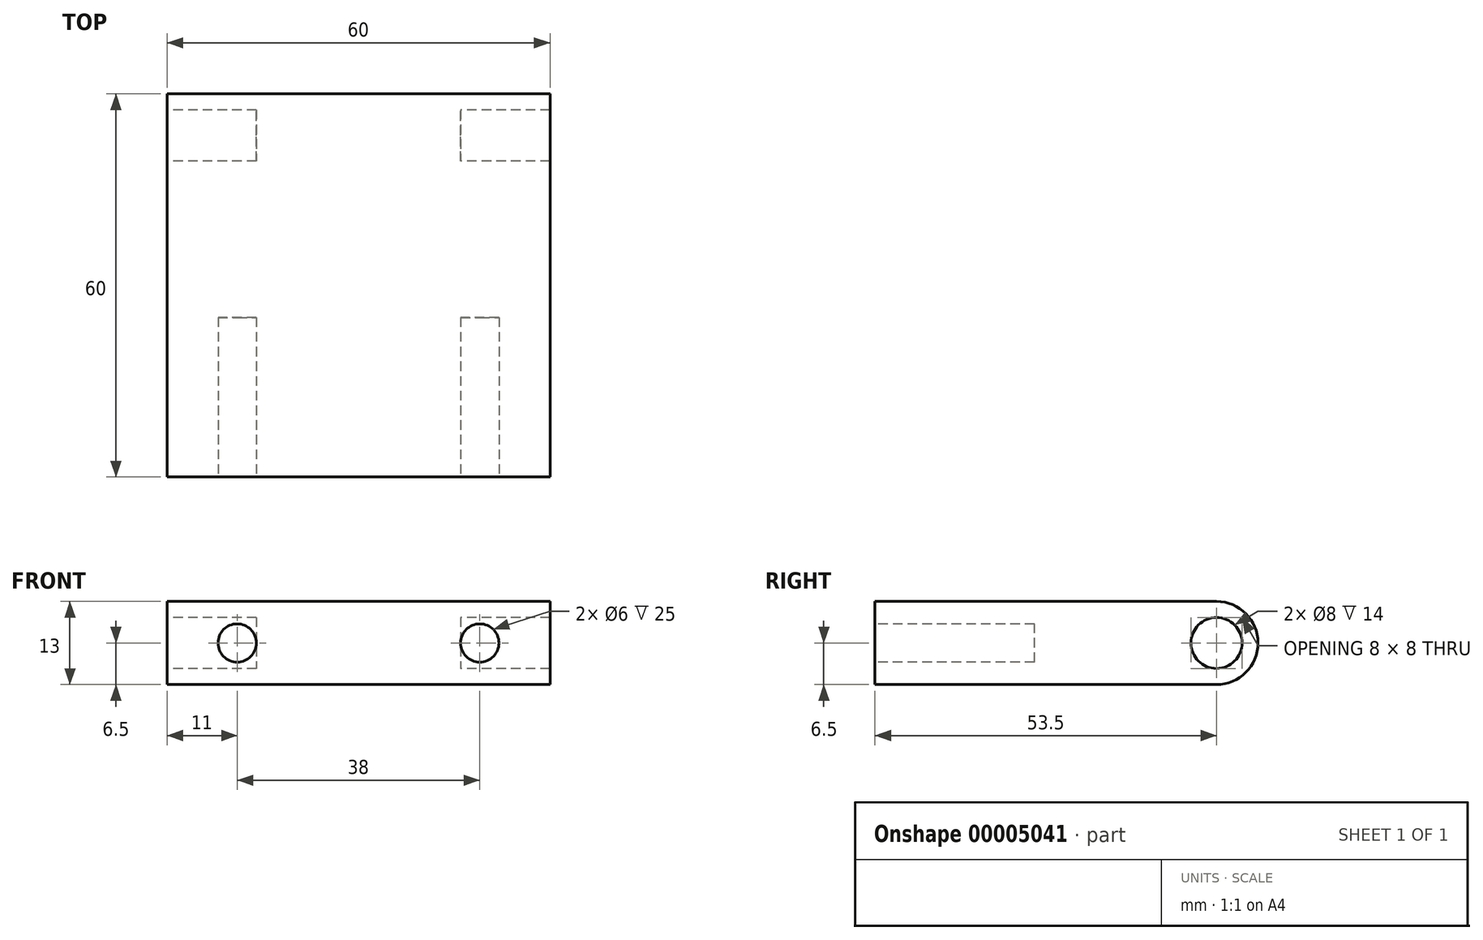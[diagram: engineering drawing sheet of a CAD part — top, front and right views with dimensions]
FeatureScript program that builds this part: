
annotation { "Feature Type Name" : "Feature", "Feature Type Description" : "" }
export const myFeature = defineFeature(function(context is Context, id is Id, definition is map)
    precondition{}
    {
        {
            var Q0;
            Q0=qCreatedBy(makeId("Top.planeOp"),FACE);
            var sketch = newSketch(context, id + "F0", { "sketchPlane" : qUnion([Q0])});
            skLineSegment(sketch, "E0.rect.bottom", {"start": v(30, 30) * mm, "end": v(-30, 30) * mm});
            skLineSegment(sketch, "E0.rect.top", {"start": v(30, -30) * mm, "end": v(-30, -30) * mm});
            skLineSegment(sketch, "E0.rect.left", {"start": v(30, 30) * mm, "end": v(30, -30) * mm});
            skLineSegment(sketch, "E0.rect.right", {"start": v(-30, 30) * mm, "end": v(-30, -30) * mm});
            skPoint(sketch, "E0.rect.middle", {"position": v(0, 0) * mm});
            skSolve(sketch);
        }
        {
            var Q0;
            Q0=makeQuery(id+"F0.imprint","IMPRINT",FACE,{"disambiguationData":[TD([[makeQuery(id+"F0.imprint","IMPRINT",EDGE,{"derivedFrom":sQuery(id+"F0.wireOp",EDGE,"E0.rect.bottom")}),1.0]])]});
            extrude(context, id + "F1", {"entities" : qUnion([Q0]), "depth" : 13 * mm});
        }
        {
            var Q0;
            Q0=makeQuery(id+"F1.opExtrude","SWEPT_FACE",FACE,{"disambiguationData":[OSD([sQuery(id+"F0.wireOp",EDGE,"E0.rect.top")])]});
            var sketch = newSketch(context, id + "F2", { "sketchPlane" : qUnion([Q0])});
            skCircle(sketch, "E1", {"center": v(-19, 6.5) * mm, "radius": 3 * mm});
            skCircle(sketch, "E2.0.MirrorC", {"center": v(19, 6.5) * mm, "radius": 3 * mm});
            skSolve(sketch);
        }
        {
            var Q0;
            Q0 = qSketchRegion(id + "F2", true);
            extrude(context, id + "F3", {"entities" : qUnion([Q0]), "operationType" : NewBodyOperationType.REMOVE, "oppositeDirection" : true, "depth" : 25 * mm});
        }
        {
            var Q0;
            Q0=makeQuery(id+"F1.opExtrude","CAP_FACE",FACE,{"disambiguationData":[OSD([sQuery(id+"F0.wireOp",EDGE,"E0.rect.bottom"),sQuery(id+"F0.wireOp",EDGE,"E0.rect.top"),sQuery(id+"F0.wireOp",EDGE,"E0.rect.left"),sQuery(id+"F0.wireOp",EDGE,"E0.rect.right")])],"isStart":false});
            var sketch = newSketch(context, id + "F4", { "sketchPlane" : qUnion([Q0])});
            skLineSegment(sketch, "E3", {"start": v(-30, 17) * mm, "end": v(-16, 17) * mm});
            skLineSegment(sketch, "E4", {"start": v(-16, 17) * mm, "end": v(-16, 30) * mm});
            skLineSegment(sketch, "E5.0.MirrorCS", {"start": v(16, 17) * mm, "end": v(16, 30) * mm});
            skLineSegment(sketch, "E5.1.MirrorCS", {"start": v(30, 17) * mm, "end": v(16, 17) * mm});
            skSolve(sketch);
        }
        {
            var Q0;
            {var subQ1=sQuery(id+"F4.wireOp",EDGE,"E3");Q0=makeQuery(id+"F4.imprint","IMPRINT",FACE,{"disambiguationData":[TD([[makeQuery(id+"F4.imprint","IMPRINT",EDGE,{"derivedFrom":subQ1}),1.0]])]});}
            var Q1;
            {var subQ4=sQuery(id+"F4.wireOp",EDGE,"E5.0.MirrorCS");Q1=makeQuery(id+"F4.imprint","IMPRINT",FACE,{"disambiguationData":[TD([[makeQuery(id+"F4.imprint","IMPRINT",EDGE,{"derivedFrom":subQ4}),-1.0]])]});}
            extrude(context, id + "F5", {"entities" : qUnion([Q0, Q1]), "operationType" : NewBodyOperationType.REMOVE, "oppositeDirection" : true, "depth" : 25 * mm});
        }
        {
            var Q0;
            Q0=makeQuery(id+"F5.boolean.opBoolean","COPY",FACE,{"derivedFrom":makeQuery(id+"F5.opExtrude","SWEPT_FACE",FACE,{"disambiguationData":[OSD([sQuery(id+"F4.wireOp",EDGE,"E4")])]})});
            var sketch = newSketch(context, id + "F6", { "sketchPlane" : qUnion([Q0])});
            skLineSegment(sketch, "E6", {"start": v(-30, 6.5) * mm, "end": v(-17, 6.5) * mm});
            skLineSegment(sketch, "E7", {"start": v(-17, 6.5) * mm, "end": v(-23.5, 6.5) * mm});
            skLineSegment(sketch, "E8", {"start": v(-23.5, 6.5) * mm, "end": v(-23.5, 13) * mm});
            skLineSegment(sketch, "E9", {"start": v(-23.5, 13) * mm, "end": v(-23.5, 0) * mm});
            skCircle(sketch, "E10", {"center": v(-23.5, 6.5) * mm, "radius": 4 * mm});
            skSolve(sketch);
        }
        {
            var Q0;
            Q0 = qSketchRegion(id + "F6", true);
            extrude(context, id + "F7", {"entities" : qUnion([Q0]), "operationType" : NewBodyOperationType.REMOVE, "oppositeDirection" : true, "depth" : 100 * mm});
        }
        {
            var Q0;
            Q0=makeQuery(id+"F5.boolean.opBoolean","COPY",FACE,{"derivedFrom":makeQuery(id+"F5.opExtrude","SWEPT_FACE",FACE,{"disambiguationData":[OSD([sQuery(id+"F4.wireOp",EDGE,"E4")])]})});
            var Q1;
            Q1=makeQuery(id+"F1.opExtrude","SWEPT_FACE",FACE,{"disambiguationData":[OSD([sQuery(id+"F0.wireOp",EDGE,"E0.rect.right")])]});
            extrude(context, id + "F8", {"entities" : qUnion([Q0]), "operationType" : NewBodyOperationType.ADD, "endBound" : BoundingType.UP_TO_SURFACE, "endBoundEntityFace" : qUnion([Q1]), "depth" : 17.1 * mm});
        }
        {
            var Q0;
            Q0=makeQuery(id+"F5.boolean.opBoolean","COPY",FACE,{"derivedFrom":makeQuery(id+"F5.opExtrude","SWEPT_FACE",FACE,{"disambiguationData":[OSD([sQuery(id+"F4.wireOp",EDGE,"E5.0.MirrorCS")])]})});
            var Q1;
            Q1=makeQuery(id+"F1.opExtrude","SWEPT_FACE",FACE,{"disambiguationData":[OSD([sQuery(id+"F0.wireOp",EDGE,"E0.rect.left")])]});
            extrude(context, id + "F9", {"entities" : qUnion([Q0]), "operationType" : NewBodyOperationType.ADD, "endBound" : BoundingType.UP_TO_SURFACE, "endBoundEntityFace" : qUnion([Q1]), "depth" : 25 * mm});
        }
        {
            var Q0;
            {var subQ0=sQuery(id+"F0.wireOp",EDGE,"E0.rect.bottom");Q0=makeQuery(id+"F9.boolean.opBoolean","MERGE",FACE,{"derivedFrom":[makeQuery(id+"F8.boolean.opBoolean","MERGE",FACE,{"derivedFrom":[makeQuery(id+"F1.opExtrude","SWEPT_FACE",FACE,{"disambiguationData":[OSD([subQ0])]}),makeQuery(id+"F8.opExtrude","SWEPT_FACE",FACE,{"disambiguationData":[OSD([subQ0,sQuery(id+"F4.wireOp",EDGE,"E4")])]})]}),makeQuery(id+"F9.opExtrude","SWEPT_FACE",FACE,{"disambiguationData":[OSD([subQ0,sQuery(id+"F4.wireOp",EDGE,"E5.0.MirrorCS")])]})]});}
            var sketch = newSketch(context, id + "F10", { "sketchPlane" : qUnion([Q0])});
            skLineSegment(sketch, "E11", {"start": v(-16, 0) * mm, "end": v(-16, 13) * mm});
            skLineSegment(sketch, "E12", {"start": v(16, 0) * mm, "end": v(16, 13) * mm});
            skSolve(sketch);
        }
        {
            var Q0;
            Q0 = qSketchRegion(id + "F10", true);
            var Q1;
            {var subQ5=sQuery(id+"F10.wireOp",EDGE,"E11");Q1=makeQuery(id+"F10.imprint","IMPRINT",FACE,{"disambiguationData":[TD([[makeQuery(id+"F10.imprint","IMPRINT",EDGE,{"derivedFrom":subQ5}),-1.0]])]});}
            extrude(context, id + "F11", {"entities" : qUnion([Q0, Q1]), "operationType" : NewBodyOperationType.ADD, "oppositeDirection" : true, "depth" : 25 * mm});
        }
        {
            var Q0;
            Q0=makeQuery(id+"F9.boolean.opBoolean","MERGE",FACE,{"derivedFrom":[makeQuery(id+"F8.boolean.opBoolean","MERGE",FACE,{"derivedFrom":[makeQuery(id+"F1.opExtrude","CAP_FACE",FACE,{"disambiguationData":[OSD([sQuery(id+"F0.wireOp",EDGE,"E0.rect.bottom"),sQuery(id+"F0.wireOp",EDGE,"E0.rect.top"),sQuery(id+"F0.wireOp",EDGE,"E0.rect.left"),sQuery(id+"F0.wireOp",EDGE,"E0.rect.right")])],"isStart":false}),makeQuery(id+"F8.opExtrude","SWEPT_FACE",FACE,{"disambiguationData":[OSD([sQuery(id+"F4.wireOp",EDGE,"E4")])]})]}),makeQuery(id+"F9.opExtrude","SWEPT_FACE",FACE,{"disambiguationData":[OSD([sQuery(id+"F4.wireOp",EDGE,"E5.0.MirrorCS")])]})]});
            var sketch = newSketch(context, id + "F12", { "sketchPlane" : qUnion([Q0])});
            skLineSegment(sketch, "E13", {"start": v(16, 30) * mm, "end": v(16, 17) * mm});
            skLineSegment(sketch, "E14", {"start": v(16, 17) * mm, "end": v(-16, 17) * mm});
            skLineSegment(sketch, "E15", {"start": v(-16, 17) * mm, "end": v(-16, 30) * mm});
            skLineSegment(sketch, "E16", {"start": v(-16, 30) * mm, "end": v(16, 30) * mm});
            skPoint(sketch, "E17", {"position": v(0, 30) * mm});
            skSolve(sketch);
        }
        {
            var Q0;
            Q0 = qSketchRegion(id + "F12", true);
            extrude(context, id + "F13", {"entities" : qUnion([Q0]), "operationType" : NewBodyOperationType.REMOVE, "oppositeDirection" : true, "depth" : 25 * mm});
        }
        {
            var Q0;
            {var subQ0=sQuery(id+"F0.wireOp",EDGE,"E0.rect.left");Q0=makeQuery(id+"F9.boolean.opBoolean","MERGE",FACE,{"derivedFrom":[makeQuery(id+"F1.opExtrude","SWEPT_FACE",FACE,{"disambiguationData":[OSD([subQ0])]}),makeQuery(id+"F9.opExtrude","CAP_FACE",FACE,{"disambiguationData":[OSD([subQ0])],"isStart":false})]});}
            var sketch = newSketch(context, id + "F14", { "sketchPlane" : qUnion([Q0])});
            skCircle(sketch, "E18", {"center": v(23.5, 6.5) * mm, "radius": 6.5 * mm});
            skSolve(sketch);
        }
        {
            var Q0;
            {var subQ0=sQuery(id+"F14.wireOp",EDGE,"E18");var subQ1=sQuery(id+"F0.wireOp",EDGE,"E0.rect.left");var subQ2=makeQuery(id+"F1.opExtrude","SWEPT_FACE",FACE,{"disambiguationData":[OSD([subQ1])]});var subQ3=sQuery(id+"F4.wireOp",EDGE,"E5.0.MirrorCS");var subQ4=makeQuery(id+"F9.boolean.opBoolean","MERGE",EDGE,{"derivedFrom":[makeQuery(id+"F1.opExtrude","CAP_EDGE",EDGE,{"disambiguationData":[OSD([subQ1])],"isStart":false}),makeQuery(id+"F9.opExtrude","TWEAK_EDGE",EDGE,{"derivedFrom":[makeQuery(id+"F5.boolean.opBoolean","COPY",EDGE,{"derivedFrom":makeQuery(id+"F5.opExtrude","CAP_EDGE",EDGE,{"disambiguationData":[OSD([subQ3])],"isStart":true})}),subQ2]})]});var subQ5=makeQuery(id+"F14.imprint","INTERSECT",VERTEX,{"derivedFrom":[subQ4,subQ0]});Q0=makeQuery(id+"F14.imprint","IMPRINT",FACE,{"disambiguationData":[TD([[makeQuery(id+"F14.imprint","IMPRINT",EDGE,{"disambiguationData":[TD([[subQ5,1.0]])],"derivedFrom":subQ0}),-1.0]])]});}
            var Q1;
            {var subQ0=sQuery(id+"F14.wireOp",EDGE,"E18");var subQ1=sQuery(id+"F0.wireOp",EDGE,"E0.rect.left");var subQ2=makeQuery(id+"F1.opExtrude","SWEPT_FACE",FACE,{"disambiguationData":[OSD([subQ1])]});var subQ3=sQuery(id+"F4.wireOp",EDGE,"E5.0.MirrorCS");var subQ4=sQuery(id+"F0.wireOp",EDGE,"E0.rect.bottom");var subQ5=makeQuery(id+"F9.opExtrude","TWEAK_EDGE",EDGE,{"derivedFrom":[makeQuery(id+"F5.boolean.opBoolean","COPY",EDGE,{"derivedFrom":makeQuery(id+"F5.opExtrude","SWEPT_EDGE",EDGE,{"disambiguationData":[OSD([subQ4,subQ3])]})}),subQ2]});var subQ6=makeQuery(id+"F14.imprint","INTERSECT",VERTEX,{"derivedFrom":[subQ5,subQ0]});Q1=makeQuery(id+"F14.imprint","IMPRINT",FACE,{"disambiguationData":[TD([[makeQuery(id+"F14.imprint","IMPRINT",EDGE,{"disambiguationData":[TD([[subQ6,1.0]])],"derivedFrom":subQ0}),-1.0]])]});}
            extrude(context, id + "F15", {"entities" : qUnion([Q0, Q1]), "operationType" : NewBodyOperationType.REMOVE, "oppositeDirection" : true, "depth" : 125 * mm});
        }
    });
